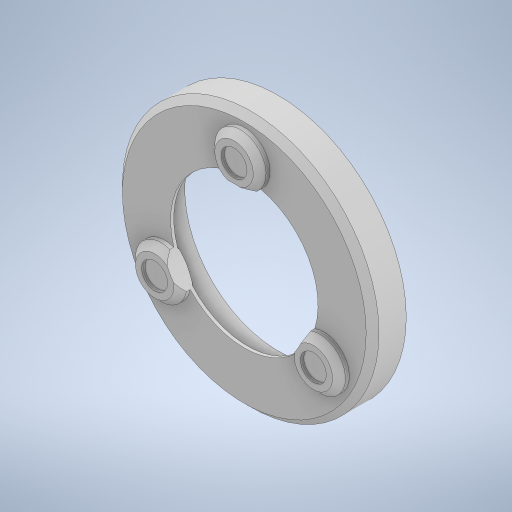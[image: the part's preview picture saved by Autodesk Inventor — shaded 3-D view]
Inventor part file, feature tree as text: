
AUTODESK INVENTOR PART (.ipt)
format: ipt  version: 2023.4 (Build 274418000, 418)  size: 458,752 bytes
history: native  units: mm
features: extrude x9, chamfer x6, projected_geometry x5, sketch x4
ambient origin geometry x8: Origin, YZ Plane, XZ Plane, XY Plane, X Axis, Y Axis, Z Axis, Center Point
bodies: Solid1 (feature_tree)
feature tree (24):
  extrude  "Extrusion1"  Depth=80.0mm
  extrude  "Extrusion2"  Depth=49.5mm
  extrude  "Extrusion3"  TaperAngle=0.0deg  [1 undecoded]
  chamfer  "Chamfer1"  Distance=16.0mm
  extrude  "Extrusion4"  Depth=10.0mm
  extrude  "Extrusion5"  Depth=10.0mm TaperAngle=360.0deg
  extrude  "Extrusion6"  Depth=10.0mm TaperAngle=0.0deg
  chamfer  "Chamfer2"  Distance=30.0mm Angle=360.0deg
  chamfer  "Chamfer3"  Distance=8.1mm
  extrude  "Extrusion7"  Depth=10.0mm TaperAngle=360.0deg
  chamfer  "Chamfer4"  Distance=1.0mm
  chamfer  "Chamfer5"  Distance=2.0mm Angle=45.0deg
  chamfer  "Chamfer6"  Distance=1.0mm
  extrude  "Extrusion8"  Depth=10.0mm
  extrude  "Extrusion9"  Depth=10.0mm TaperAngle=0.0deg
  sketch  "Sketch2"  dims[d0=58.1mm d1=80.0mm]
  projected_geometry  "Projected Loop1"
  projected_geometry  "Projected Loop2"
  projected_geometry  "Projected Loop3"
  projected_geometry  "Projected Loop4"
  projected_geometry  "Projected Loop5"
  sketch  "Sketch7"  dims[d2=7.0mm d3=0.0mm d4=49.5mm]
  sketch  "Sketch8"  dims[d5=0.0mm d6=0.0mm]
  sketch  "Sketch10"  dims[d7=0.0mm d8=16.0mm d9=8.1mm d10=30.0mm d12=360.0deg d14=6.7mm d15=0.0mm d17=30.0mm d19=360.0deg d21=8.1mm d22=30.0mm d24=360.0deg d26=1.0mm d27=0.0mm d28=2.0mm d29=2.0mm d30=45.0deg d31=1.0mm d32=0.0mm d33=1.5mm d34=3.5mm d35=0.0mm d36=0.0mm d37=0.0mm d38=3.0mm d39=2.0mm d40=45.0deg d41=3.0mm d42=2.0mm d43=45.0deg d44=1.0mm d45=0.0mm d46=2.0mm d47=2.0mm d48=45.0deg d49=0.4mm d50=2.0mm d51=45.0deg d52=1.0mm d53=2.0mm d54=45.0deg d55=44.0mm d56=0.0mm d57=0.0mm d58=46.0mm d59=10.0mm d60=0.0mm]
note: 1 required parameter value undecoded (feature->parameter linkage not recoverable at this tier; creation-order binding heuristic only, values carry confidence <= 0.55)
